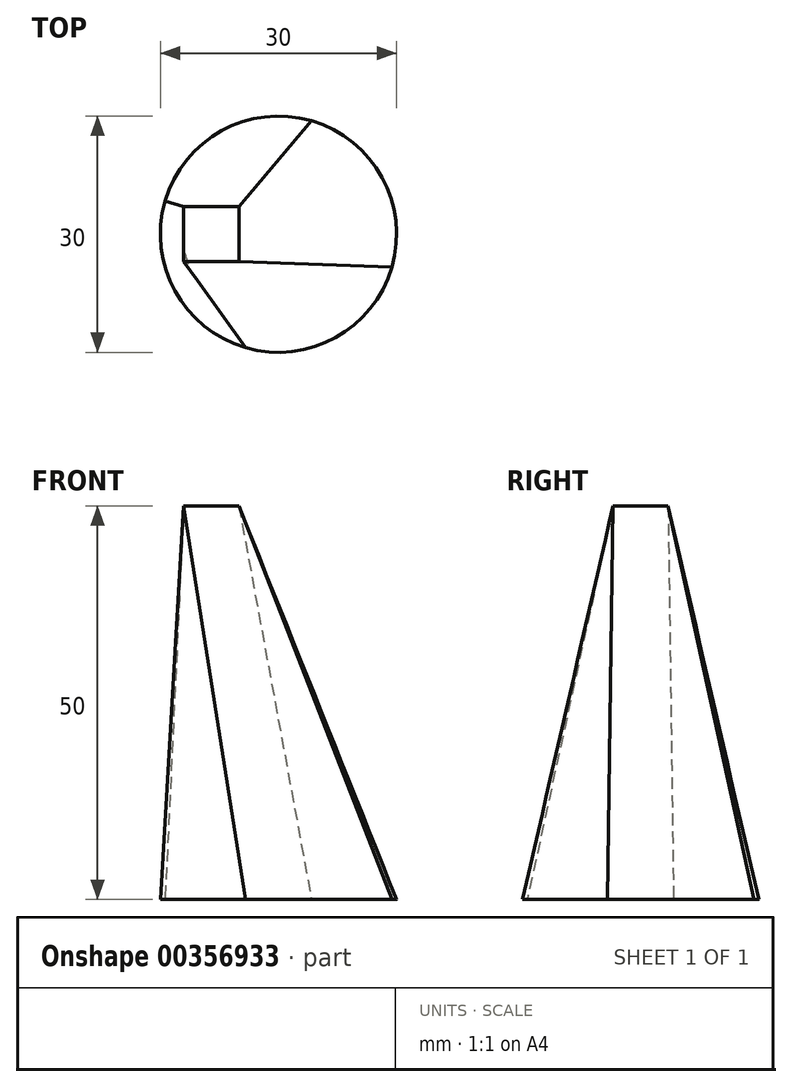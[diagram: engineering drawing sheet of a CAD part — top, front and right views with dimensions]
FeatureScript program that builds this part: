
annotation { "Feature Type Name" : "Feature", "Feature Type Description" : "" }
export const myFeature = defineFeature(function(context is Context, id is Id, definition is map)
    precondition{}
    {
        {
            var Q0;
            Q0=qCreatedBy(makeId("Top.planeOp"),FACE);
            var sketch = newSketch(context, id + "F0", { "sketchPlane" : qUnion([Q0])});
            skLineSegment(sketch, "E0.bottom", {"start": v(0, 3.5) * mm, "end": v(7, 3.5) * mm});
            skLineSegment(sketch, "E0.top", {"start": v(0, -3.5) * mm, "end": v(7, -3.5) * mm});
            skLineSegment(sketch, "E0.left", {"start": v(0, 3.5) * mm, "end": v(0, -3.5) * mm});
            skLineSegment(sketch, "E0.right", {"start": v(7, 3.5) * mm, "end": v(7, -3.5) * mm});
            skSolve(sketch);
        }
        {
            var Q0;
            Q0=qCreatedBy(makeId("Top.planeOp"),FACE);
            cPlane(context, id + "F1", {"entities" : qUnion([Q0]), "cplaneType" : CPlaneType.OFFSET, "offset" : 50 * mm, "oppositeDirection" : true, "width" : 150 * mm, "height" : 150 * mm});
        }
        {
            var Q0;
            Q0=qCreatedBy(id+"F1.planeOp",FACE);
            var sketch = newSketch(context, id + "F2", { "sketchPlane" : qUnion([Q0])});
            skCircle(sketch, "E1", {"center": v(12.04, 0) * mm, "radius": 15 * mm});
            skLineSegment(sketch, "E2", {"start": v(12.04, 0) * mm, "end": v(4.11, 15.76) * mm, "construction": true});
            skLineSegment(sketch, "E3", {"start": v(12.04, 0) * mm, "end": v(27.8, 15.76) * mm, "construction": true});
            skLineSegment(sketch, "E4", {"start": v(12.04, 0) * mm, "end": v(28.45, -17.6) * mm, "construction": true});
            skLineSegment(sketch, "E5", {"start": v(12.04, 0) * mm, "end": v(4.11, -7.92) * mm, "construction": true});
            skLineSegment(sketch, "E6", {"start": v(0, 0) * mm, "end": v(46.4, 0) * mm, "construction": true});
            skPoint(sketch, "E7", {"position": v(22.64, 10.6) * mm});
            skSolve(sketch);
        }
        {
            var Q0;
            Q0 = qSketchRegion(id + "F0", true);
            var Q1;
            Q1 = qSketchRegion(id + "F2", true);
            loft(context, id + "F3", {"sheetProfilesArray" : [{ "sheetProfileEntities" : qUnion([Q0]) }, { "sheetProfileEntities" : qUnion([Q1]) }]});
        }
    });
